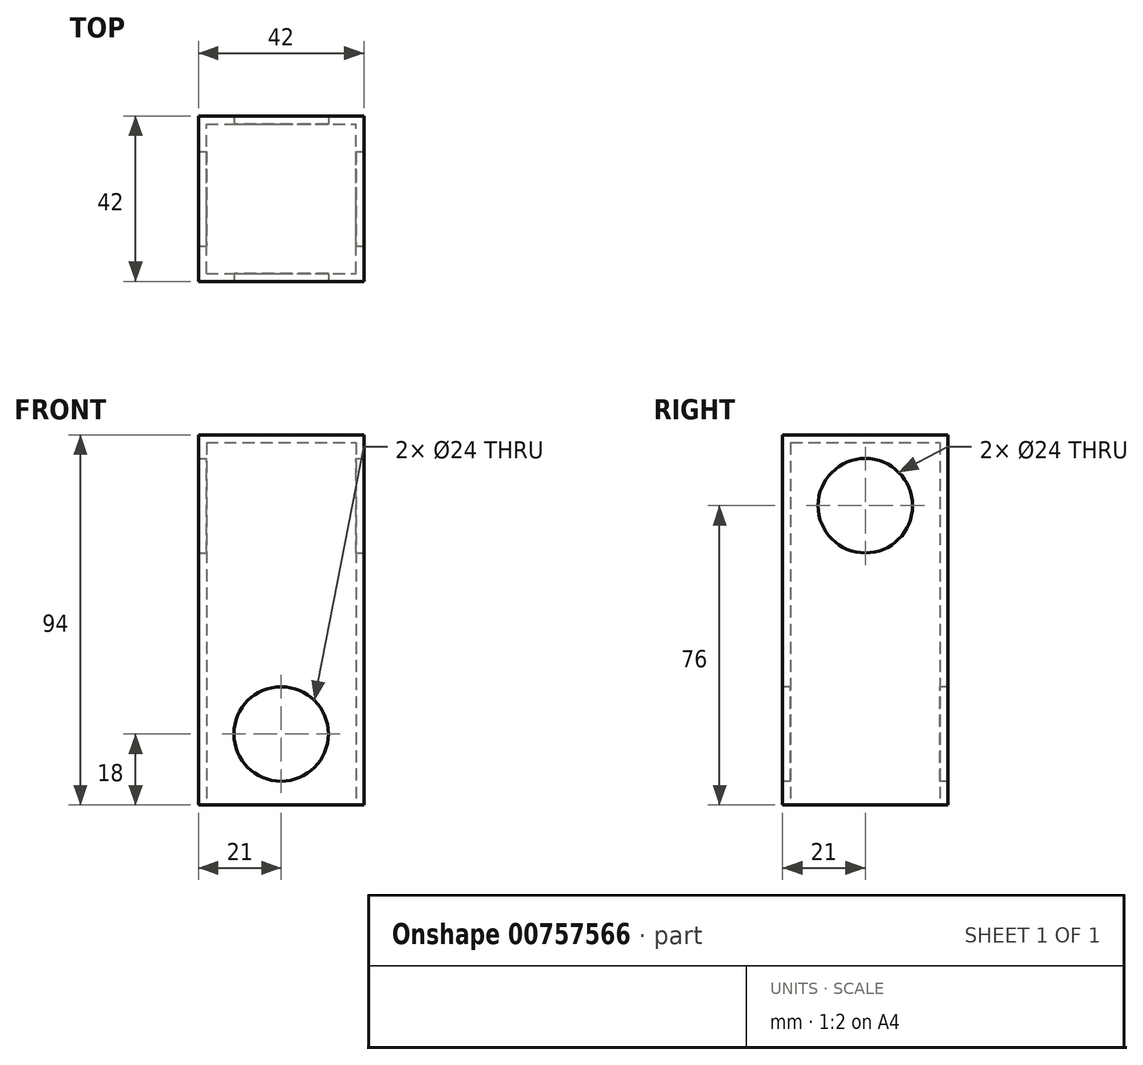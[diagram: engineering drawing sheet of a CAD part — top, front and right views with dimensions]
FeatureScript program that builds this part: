
annotation { "Feature Type Name" : "Feature", "Feature Type Description" : "" }
export const myFeature = defineFeature(function(context is Context, id is Id, definition is map)
    precondition{}
    {
        {
            var Q0;
            Q0=qCreatedBy(makeId("Front.planeOp"),FACE);
            var sketch = newSketch(context, id + "F0", { "sketchPlane" : qUnion([Q0])});
            skLineSegment(sketch, "E0.bottom", {"start": v(-21, 47) * mm, "end": v(21, 47) * mm});
            skLineSegment(sketch, "E0.top", {"start": v(-21, -47) * mm, "end": v(21, -47) * mm});
            skLineSegment(sketch, "E0.left", {"start": v(-21, 47) * mm, "end": v(-21, -47) * mm});
            skLineSegment(sketch, "E0.right", {"start": v(21, 47) * mm, "end": v(21, -47) * mm});
            skPoint(sketch, "E0.middle", {"position": v(0, 0) * mm});
            skPoint(sketch, "E1", {"position": v(0, -29) * mm});
            skSolve(sketch);
        }
        {
            var Q0;
            Q0 = qSketchRegion(id + "F0", true);
            extrude(context, id + "F1", {"entities" : qUnion([Q0]), "endBound" : BoundingType.SYMMETRIC, "depth" : 42 * mm, "offsetDistance" : 25.4 * mm});
        }
        {
            var Q0;
            Q0=qCreatedBy(makeId("Front.planeOp"),FACE);
            var sketch = newSketch(context, id + "F2", { "sketchPlane" : qUnion([Q0])});
            skPoint(sketch, "E2", {"position": v(0, -29) * mm});
            skCircle(sketch, "E3", {"center": v(0, -29) * mm, "radius": 12 * mm});
            skSolve(sketch);
        }
        {
            var Q0;
            Q0=makeQuery(id+"F1.opExtrude","SWEPT_FACE",FACE,{"disambiguationData":[OSD([sQuery(id+"F0.wireOp",EDGE,"E0.top")])]});
            shell(context, id + "F3", {"entities" : qUnion([Q0]), "thickness" : 2 * mm});
        }
        {
            var Q0;
            Q0 = qSketchRegion(id + "F2", true);
            extrude(context, id + "F4", {"entities" : qUnion([Q0]), "operationType" : NewBodyOperationType.REMOVE, "endBound" : BoundingType.SYMMETRIC, "oppositeDirection" : true, "depth" : 76.2 * mm, "offsetDistance" : 25.4 * mm});
        }
        {
            var Q0;
            Q0=qCreatedBy(makeId("Right.planeOp"),FACE);
            var sketch = newSketch(context, id + "F5", { "sketchPlane" : qUnion([Q0])});
            skPoint(sketch, "E4", {"position": v(0, 29) * mm});
            skCircle(sketch, "E5", {"center": v(0, 29) * mm, "radius": 12 * mm});
            skSolve(sketch);
        }
        {
            var Q0;
            Q0 = qSketchRegion(id + "F5", true);
            extrude(context, id + "F6", {"entities" : qUnion([Q0]), "operationType" : NewBodyOperationType.REMOVE, "endBound" : BoundingType.SYMMETRIC, "oppositeDirection" : true, "depth" : 76.2 * mm, "offsetDistance" : 25.4 * mm});
        }
    });
